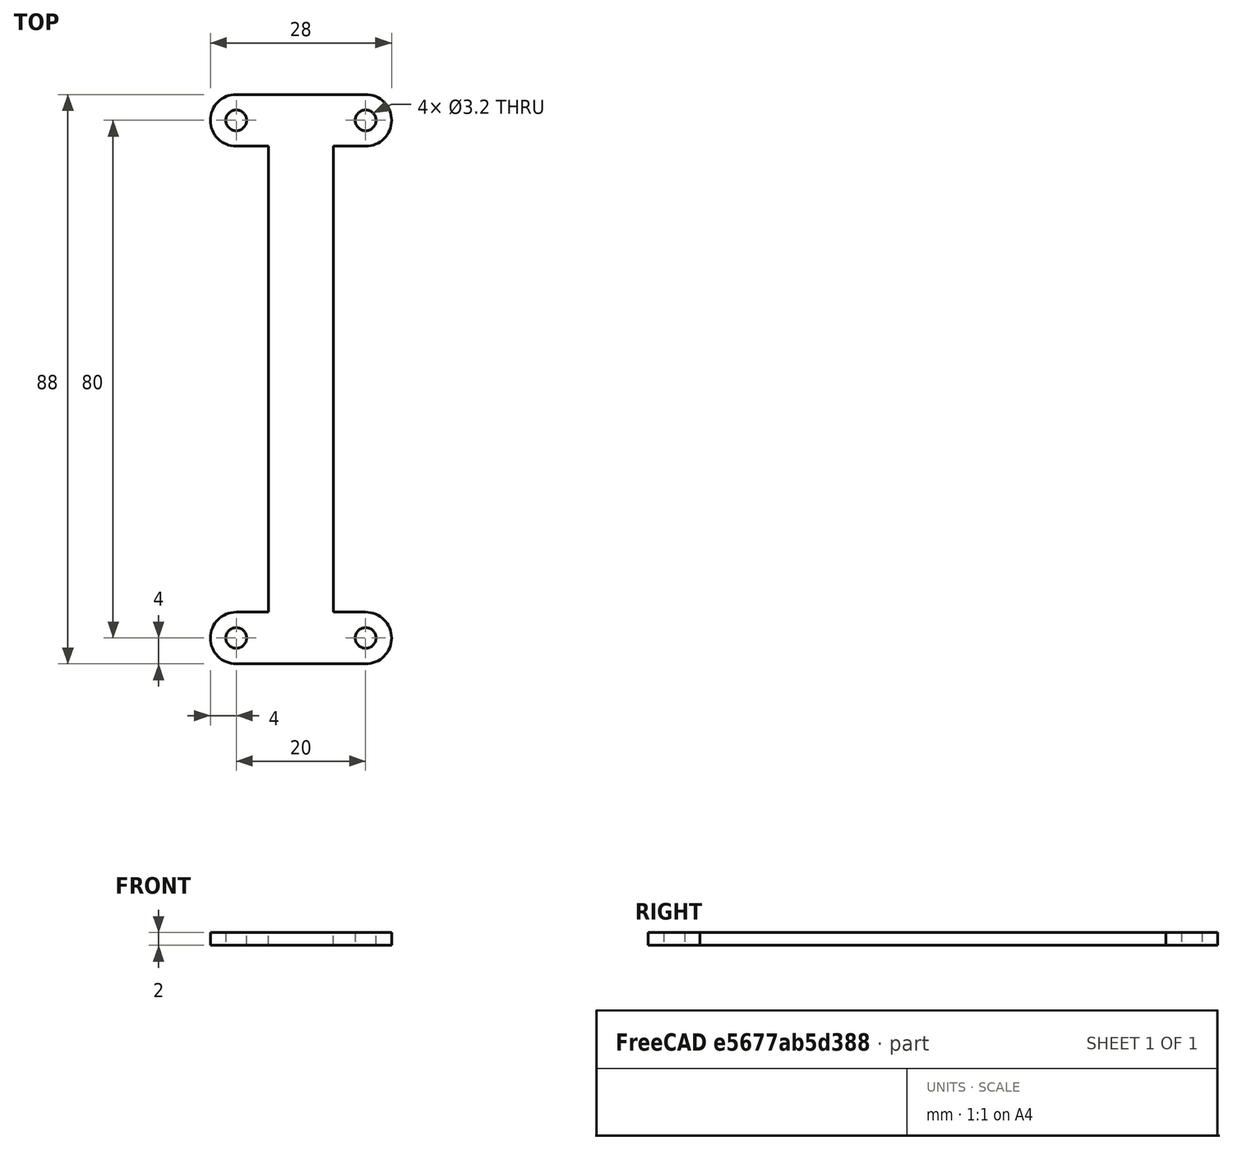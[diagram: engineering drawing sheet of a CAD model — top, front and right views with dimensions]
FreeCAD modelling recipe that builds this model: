
FCSTD DOCUMENT  (FreeCAD 0.16R6703 (Git))
Label: sensor board holder
License: All rights reserved
LicenseURL: http://en.wikipedia.org/wiki/All_rights_reserved
objects: Sketcher::SketchObject×1, PartDesign::Pad×1
note: 3 computed .brp shape members not serialized (recipe doc carries the construction recipe); baked Part::Feature solids carry a one-line shape summary decoded from their .brp

FEATURE [Sketcher::SketchObject] Sketch
  sketch-geometry (16):
    g0: Circle CenterX=10 CenterY=40 CenterZ=0 NormalX=0 NormalY=0 NormalZ=1 Radius=1.6
    g1: Circle CenterX=-10 CenterY=40 CenterZ=0 NormalX=0 NormalY=0 NormalZ=1 Radius=1.6
    g2: Circle CenterX=-10 CenterY=-40 CenterZ=0 NormalX=0 NormalY=0 NormalZ=1 Radius=1.6
    g3: Circle CenterX=10 CenterY=-40 CenterZ=0 NormalX=0 NormalY=0 NormalZ=1 Radius=1.6
    g4: ArcOfCircle CenterX=-10 CenterY=40 CenterZ=0 NormalX=0 NormalY=0 NormalZ=1 Radius=4 StartAngle=1.5708 EndAngle=4.71239
    g5: ArcOfCircle CenterX=10 CenterY=40 CenterZ=0 NormalX=0 NormalY=0 NormalZ=1 Radius=4 StartAngle=4.71239 EndAngle=7.85398
    g6: ArcOfCircle CenterX=-10 CenterY=-40 CenterZ=0 NormalX=0 NormalY=0 NormalZ=1 Radius=4 StartAngle=1.5708 EndAngle=4.71239
    g7: ArcOfCircle CenterX=10 CenterY=-40 CenterZ=0 NormalX=0 NormalY=0 NormalZ=1 Radius=4 StartAngle=4.71239 EndAngle=7.85398
    g8: LineSegment StartX=-10 StartY=-44 StartZ=0 EndX=10 EndY=-44 EndZ=0
    g9: LineSegment StartX=-10 StartY=44 StartZ=0 EndX=10 EndY=44 EndZ=0
    g10: LineSegment StartX=-10 StartY=36 StartZ=0 EndX=-5 EndY=36 EndZ=0
    g11: LineSegment StartX=10 StartY=36 StartZ=0 EndX=5 EndY=36 EndZ=0
    g12: LineSegment StartX=-10 StartY=-36 StartZ=0 EndX=-5 EndY=-36 EndZ=0
    g13: LineSegment StartX=10 StartY=-36 StartZ=0 EndX=5 EndY=-36 EndZ=0
    g14: LineSegment StartX=-5 StartY=36 StartZ=0 EndX=-5 EndY=-36 EndZ=0
    g15: LineSegment StartX=5 StartY=-36 StartZ=0 EndX=5 EndY=36 EndZ=0
  constraints (44):
    c: Radius(g0) = 1.6
    c: Equal(g0,g1)
    c: Equal(g0,g2)
    c: Equal(g0,g3)
    c: Symmetric(g1,g0,g-2)
    c: Symmetric(g2,g3,g-2)
    c: Symmetric(g0,g3,g-1)
    c: DistanceY(g2,g1) = 80
    c: DistanceX(g1,g0) = 20
    c: Coincident(g4,g1)
    c: Coincident(g5,g0)
    c: Coincident(g6,g2)
    c: Coincident(g7,g3)
    c: Coincident(g8,g6)
    c: Coincident(g8,g7)
    c: Horizontal(g8)
    c: Coincident(g9,g4)
    c: Coincident(g9,g5)
    c: Horizontal(g9)
    c: Symmetric(g6,g7,g-2)
    c: Symmetric(g6,g4,g-1)
    c: Symmetric(g6,g7,g-2)
    c: Symmetric(g4,g5,g-2)
    c: Radius(g5) = 4
    c: DistanceX(g6,g7) = 20
    c: DistanceX(g4,g5) = 20
    c: DistanceX(g4,g5) = 20
    c: Coincident(g10,g4)
    c: Horizontal(g10)
    c: Coincident(g11,g5)
    c: Horizontal(g11)
    c: Coincident(g12,g6)
    c: Horizontal(g12)
    c: Coincident(g13,g7)
    c: Horizontal(g13)
    c: Coincident(g14,g10)
    c: Coincident(g14,g12)
    c: Vertical(g14)
    c: Coincident(g15,g11)
    c: Vertical(g15)
    c: Symmetric(g13,g12,g-2)
    c: Coincident(g15,g13)
    c: Symmetric(g7,g5,g-1)
    c: DistanceX(g12,g13) = 10
FEATURE [PartDesign::Pad] Pad
  Length = 2
  Length2 = 100
  Sketch = -> Sketch
  Type = 0
